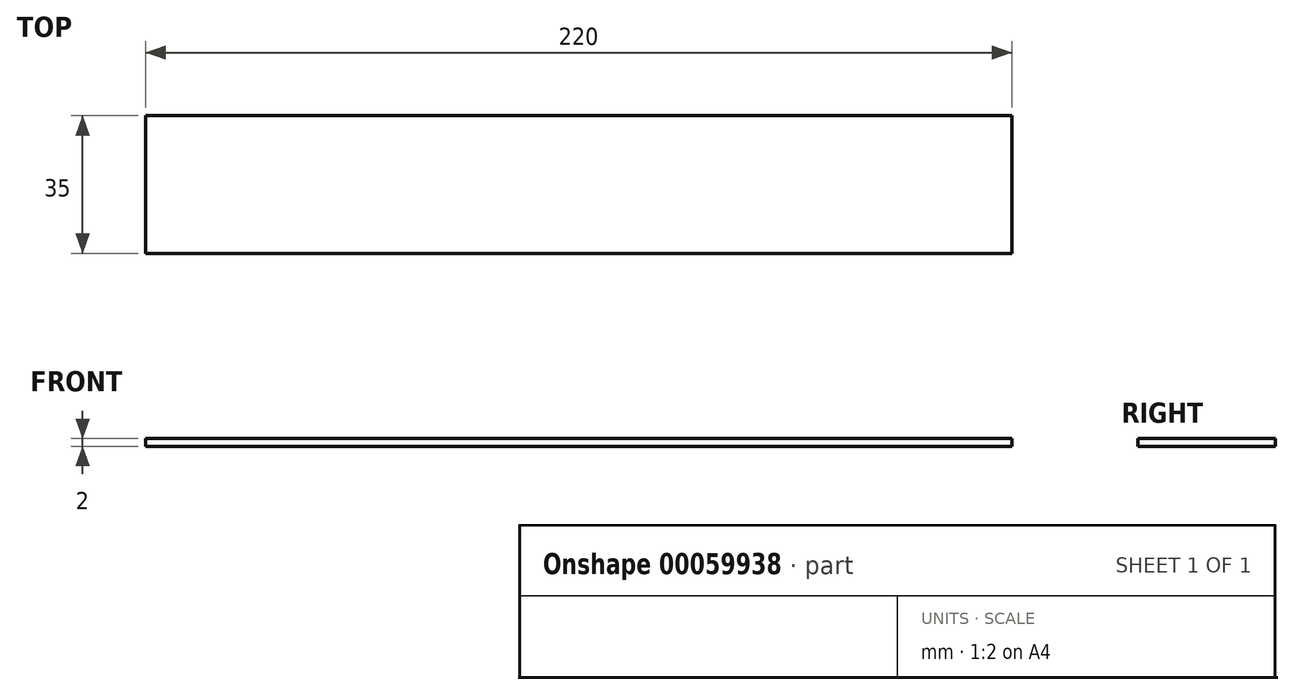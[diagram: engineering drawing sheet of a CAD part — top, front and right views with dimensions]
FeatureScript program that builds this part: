
annotation { "Feature Type Name" : "Feature", "Feature Type Description" : "" }
export const myFeature = defineFeature(function(context is Context, id is Id, definition is map)
    precondition{}
    {
        {
            var Q0;
            Q0=qCreatedBy(makeId("Top.planeOp"),FACE);
            var sketch = newSketch(context, id + "F0", { "sketchPlane" : qUnion([Q0])});
            skLineSegment(sketch, "E0.bottom", {"start": v(0, 0) * mm, "end": v(220, 0) * mm});
            skLineSegment(sketch, "E0.top", {"start": v(0, 35) * mm, "end": v(220, 35) * mm});
            skLineSegment(sketch, "E0.left", {"start": v(0, 0) * mm, "end": v(0, 35) * mm});
            skLineSegment(sketch, "E0.right", {"start": v(220, 0) * mm, "end": v(220, 35) * mm});
            skSolve(sketch);
        }
        {
            var Q0;
            Q0=makeQuery(id+"F0.imprint","IMPRINT",FACE,{"disambiguationData":[TD([[makeQuery(id+"F0.imprint","IMPRINT",EDGE,{"derivedFrom":sQuery(id+"F0.wireOp",EDGE,"E0.bottom")}),1.0]])]});
            extrude(context, id + "F1", {"entities" : qUnion([Q0]), "depth" : 2 * mm});
        }
    });
